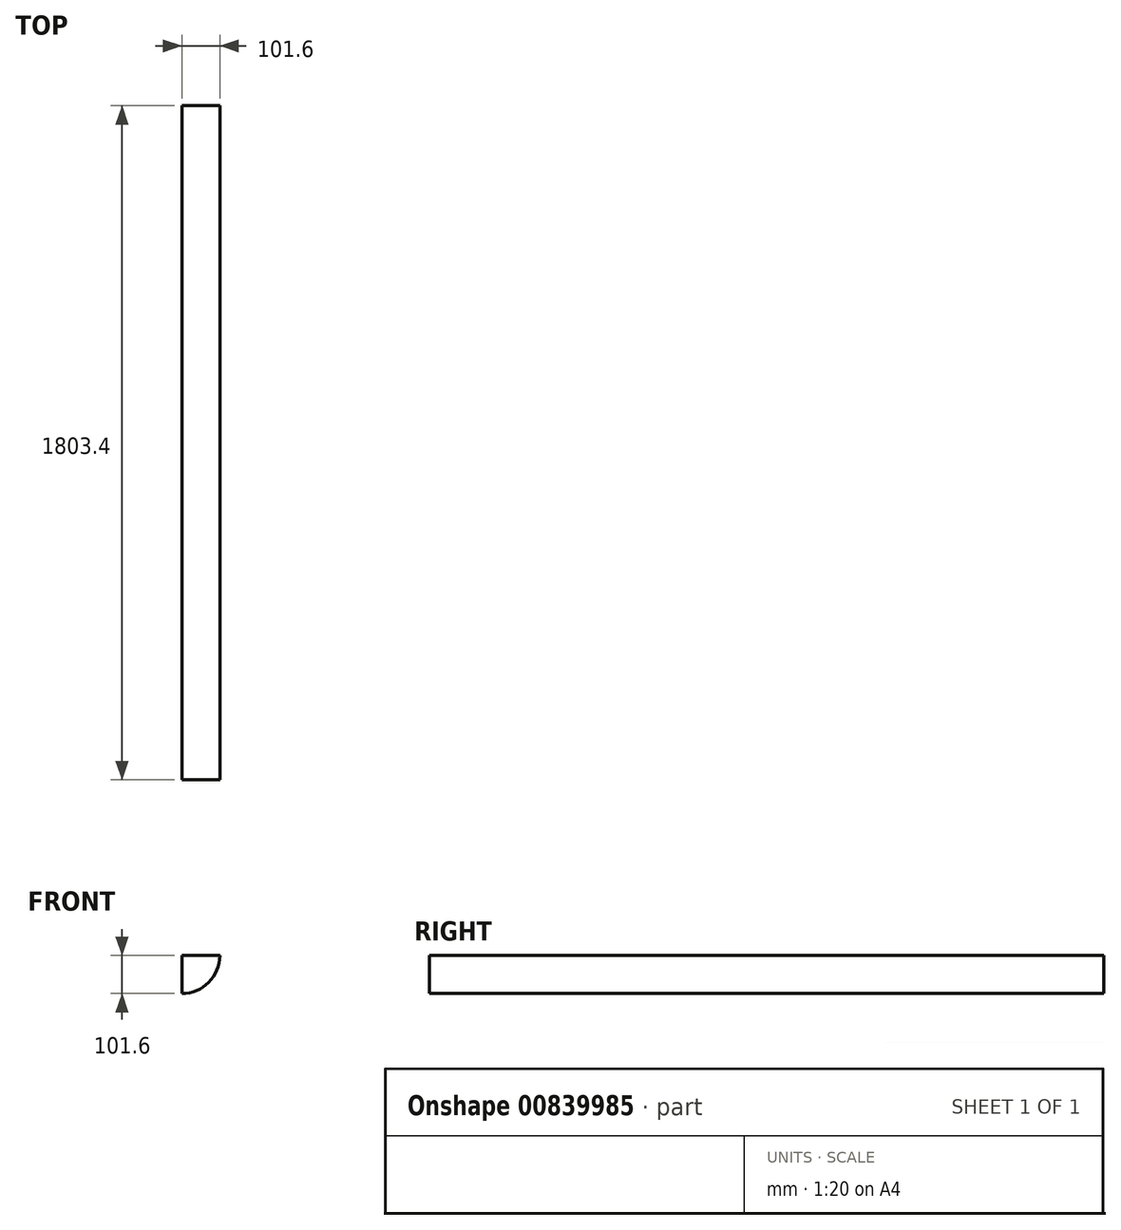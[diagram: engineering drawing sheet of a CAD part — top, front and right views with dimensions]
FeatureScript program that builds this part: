
annotation { "Feature Type Name" : "Feature", "Feature Type Description" : "" }
export const myFeature = defineFeature(function(context is Context, id is Id, definition is map)
    precondition{}
    {
        {
            var Q0;
            Q0=qCreatedBy(makeId("Front.planeOp"),FACE);
            var sketch = newSketch(context, id + "F0", { "sketchPlane" : qUnion([Q0])});
            skArc(sketch, "E0", {"start": v(0, -101.6) * mm, "mid": v(71.84, -71.84) * mm, "end": v(101.6, 0) * mm});
            skLineSegment(sketch, "E1", {"start": v(0, 0) * mm, "end": v(101.6, 0) * mm});
            skLineSegment(sketch, "E2", {"start": v(0, 0) * mm, "end": v(0, -101.6) * mm});
            skSolve(sketch);
        }
        {
            var Q0;
            Q0=qSketchRegion(id+"F0",true);
            extrude(context, id + "F1", {"entities" : qUnion([Q0]), "depth" : 1803.4 * mm, "offsetDistance" : 25.4 * mm});
        }
    });
